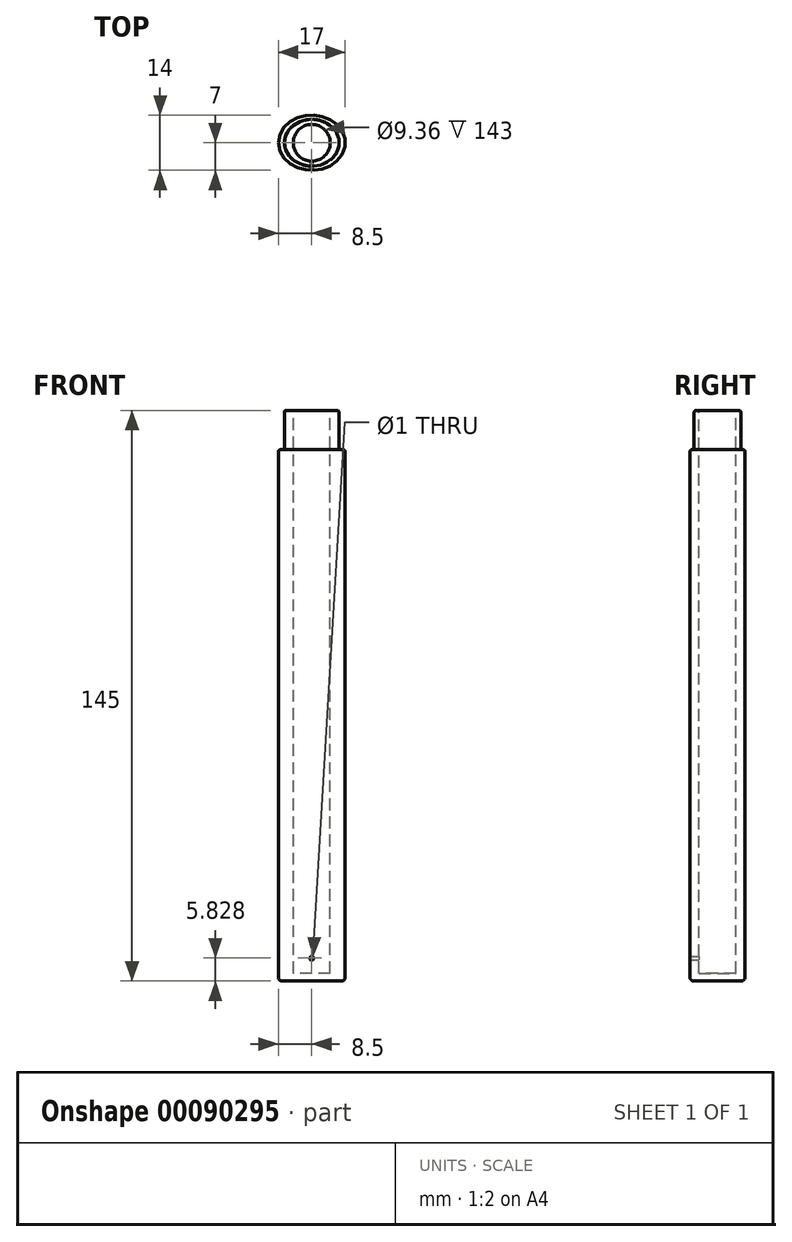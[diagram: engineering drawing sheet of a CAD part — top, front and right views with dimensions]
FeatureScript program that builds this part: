
annotation { "Feature Type Name" : "Feature", "Feature Type Description" : "" }
export const myFeature = defineFeature(function(context is Context, id is Id, definition is map)
    precondition{}
    {
        {
            var Q0;
            Q0=qCreatedBy(makeId("Top.planeOp"),FACE);
            var sketch = newSketch(context, id + "F0", { "sketchPlane" : qUnion([Q0])});
            skEllipse(sketch, "E0", {"center": v(0, 0) * mm, "majorRadius": 8.5 * mm, "minorRadius": 7 * mm, "majorAxis": v(-1, 0)});
            skCircle(sketch, "E1", {"center": v(0, 0) * mm, "radius": 4.55 * mm});
            skSolve(sketch);
        }
        {
            var Q0;
            Q0 = qSketchRegion(id + "F0", true);
            var Q1;
            Q1=makeQuery(id+"F0.imprint","IMPRINT",FACE,{"disambiguationData":[TD([[makeQuery(id+"F0.imprint","IMPRINT",EDGE,{"derivedFrom":sQuery(id+"F0.wireOp",EDGE,"E1")}),1.0]])]});
            extrude(context, id + "F1", {"entities" : qUnion([Q0, Q1]), "depth" : 135 * mm});
        }
        {
            var Q0;
            Q0=makeQuery(id+"F1.opExtrude","CAP_FACE",FACE,{"disambiguationData":[OSD([sQuery(id+"F0.wireOp",EDGE,"E0")])],"isStart":false});
            var sketch = newSketch(context, id + "F2", { "sketchPlane" : qUnion([Q0])});
            skEllipse(sketch, "E2", {"center": v(0, 0) * mm, "majorRadius": 6.95 * mm, "minorRadius": 5.95 * mm, "majorAxis": v(-1, 0)});
            skSolve(sketch);
        }
        {
            var Q0;
            Q0=makeQuery(id+"F2.imprint","IMPRINT",FACE,{"disambiguationData":[TD([[makeQuery(id+"F2.imprint","IMPRINT",EDGE,{"derivedFrom":sQuery(id+"F2.wireOp",EDGE,"E2")}),1.0]])]});
            extrude(context, id + "F3", {"entities" : qUnion([Q0]), "operationType" : NewBodyOperationType.ADD, "depth" : 10 * mm});
        }
        {
            var Q0;
            Q0=makeQuery(id+"F3.opExtrude","CAP_FACE",FACE,{"disambiguationData":[OSD([sQuery(id+"F2.wireOp",EDGE,"E2")])],"isStart":false});
            var sketch = newSketch(context, id + "F4", { "sketchPlane" : qUnion([Q0])});
            skCircle(sketch, "E3", {"center": v(0, 0) * mm, "radius": 4.68 * mm});
            skSolve(sketch);
        }
        {
            var Q0;
            Q0=makeQuery(id+"F4.imprint","IMPRINT",FACE,{"disambiguationData":[TD([[makeQuery(id+"F4.imprint","IMPRINT",EDGE,{"derivedFrom":sQuery(id+"F4.wireOp",EDGE,"E3")}),1.0]])]});
            extrude(context, id + "F5", {"entities" : qUnion([Q0]), "operationType" : NewBodyOperationType.REMOVE, "oppositeDirection" : true, "depth" : 143 * mm});
        }
        {
            var Q0;
            Q0=makeQuery(id+"F5.boolean.opBoolean","COPY",EDGE,{"derivedFrom":makeQuery(id+"F5.opExtrude","CAP_EDGE",EDGE,{"disambiguationData":[OSD([sQuery(id+"F4.wireOp",EDGE,"E3")])],"isStart":true})});
            var Q1;
            Q1=makeQuery(id+"F3.opExtrude","CAP_EDGE",EDGE,{"disambiguationData":[OSD([sQuery(id+"F2.wireOp",EDGE,"E2")])],"isStart":false});
            var Q2;
            Q2=makeQuery(id+"F1.opExtrude","CAP_EDGE",EDGE,{"disambiguationData":[OSD([sQuery(id+"F0.wireOp",EDGE,"E0")])],"isStart":false});
            fillet(context, id + "F6", {"entities" : qUnion([Q0, Q1, Q2]), "radius" : .5 * mm, "tangentPropagation" : true, "allowEdgeOverflow" : false});
        }
        {
            var Q0;
            Q0=makeQuery(id+"F1.opExtrude","CAP_EDGE",EDGE,{"disambiguationData":[OSD([sQuery(id+"F0.wireOp",EDGE,"E0")])],"isStart":true});
            fillet(context, id + "F7", {"entities" : qUnion([Q0]), "radius" : 1 * mm, "tangentPropagation" : true, "allowEdgeOverflow" : false});
        }
        {
            var Q0;
            Q0=qCreatedBy(makeId("Front.planeOp"),FACE);
            var sketch = newSketch(context, id + "F8", { "sketchPlane" : qUnion([Q0])});
            skCircle(sketch, "E4", {"center": v(0, 5.83) * mm, "radius": 0.5 * mm});
            skSolve(sketch);
        }
        {
            var Q0;
            Q0 = qSketchRegion(id + "F8", true);
            extrude(context, id + "F9", {"entities" : qUnion([Q0]), "operationType" : NewBodyOperationType.REMOVE, "depth" : 25 * mm});
        }
    });
